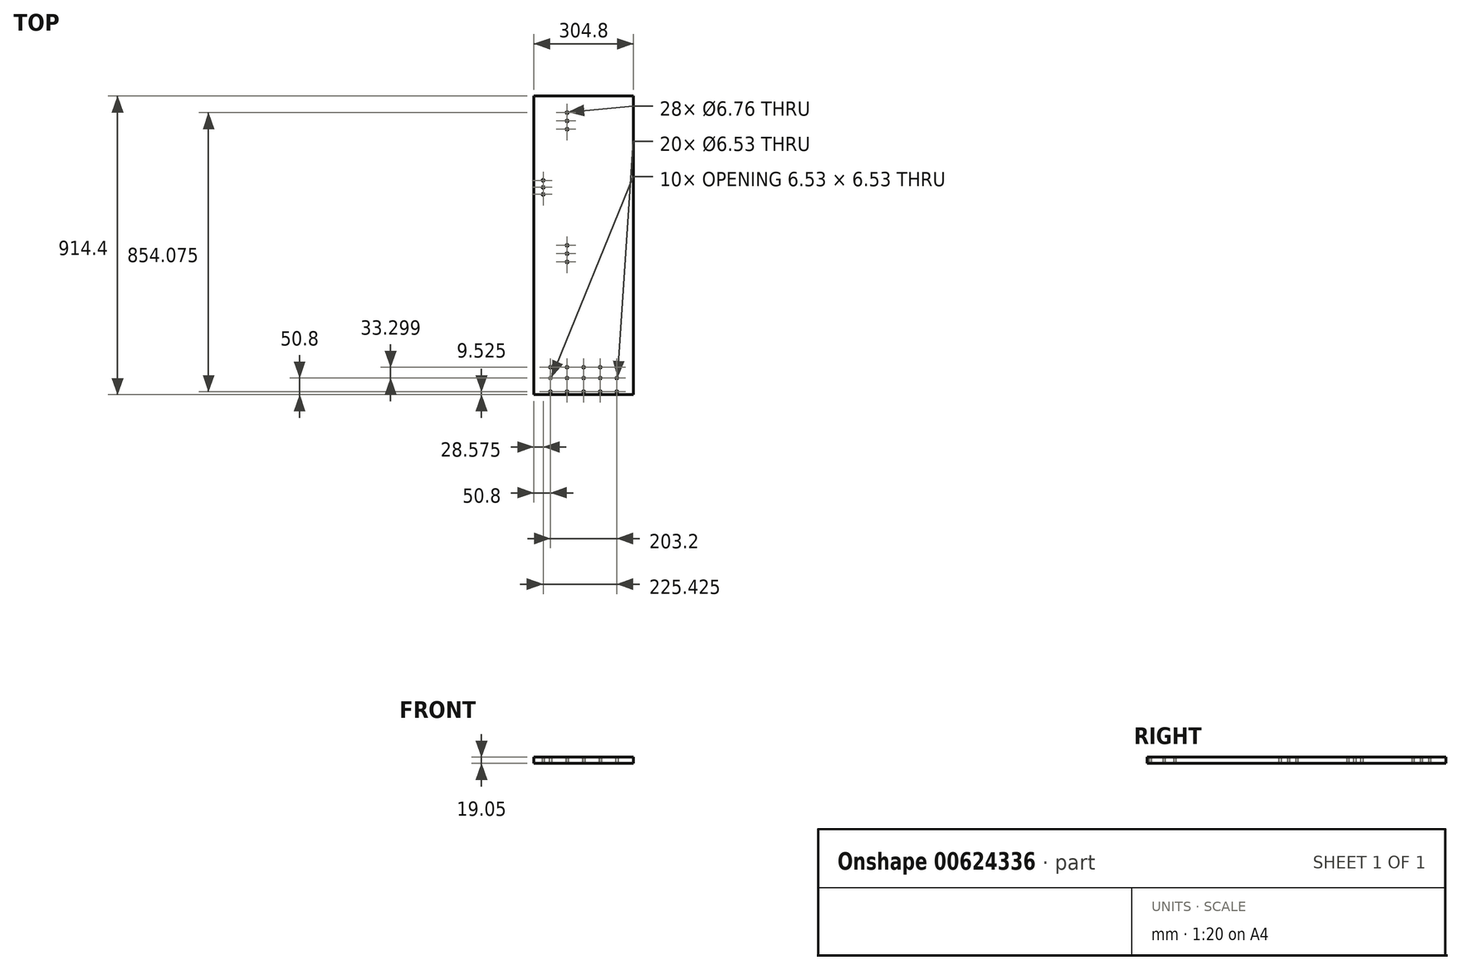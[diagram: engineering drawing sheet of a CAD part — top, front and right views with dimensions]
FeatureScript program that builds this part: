
annotation { "Feature Type Name" : "Feature", "Feature Type Description" : "" }
export const myFeature = defineFeature(function(context is Context, id is Id, definition is map)
    precondition{}
    {
        {
            var Q0;
            Q0=qCreatedBy(makeId("Top.planeOp"),FACE);
            var sketch = newSketch(context, id + "F0", { "sketchPlane" : qUnion([Q0])});
            skLineSegment(sketch, "E0.bottom", {"start": v(0, 0) * mm, "end": v(-304.8, 0) * mm});
            skLineSegment(sketch, "E0.top", {"start": v(0, 914.4) * mm, "end": v(-304.8, 914.4) * mm});
            skLineSegment(sketch, "E0.left", {"start": v(0, 0) * mm, "end": v(0, 914.4) * mm});
            skLineSegment(sketch, "E0.right", {"start": v(-304.8, 0) * mm, "end": v(-304.8, 914.4) * mm});
            skLineSegment(sketch, "E1", {"start": v(-203.2, 914.4) * mm, "end": v(-203.2, 0) * mm, "construction": true});
            skLineSegment(sketch, "E2", {"start": v(-304.8, 635) * mm, "end": v(0, 635) * mm, "construction": true});
            skCircle(sketch, "E3", {"center": v(-203.2, 863.6) * mm, "radius": 3.38 * mm});
            skCircle(sketch, "E4", {"center": v(-203.2, 838.2) * mm, "radius": 3.38 * mm});
            skCircle(sketch, "E5", {"center": v(-203.2, 812.8) * mm, "radius": 3.38 * mm});
            skCircle(sketch, "E6", {"center": v(-203.2, 457.2) * mm, "radius": 3.38 * mm});
            skCircle(sketch, "E7", {"center": v(-203.2, 431.8) * mm, "radius": 3.38 * mm});
            skCircle(sketch, "E8", {"center": v(-203.2, 406.4) * mm, "radius": 3.38 * mm});
            skLineSegment(sketch, "E9", {"start": v(-304.8, 9.52) * mm, "end": v(0, 9.52) * mm, "construction": true});
            skCircle(sketch, "E10", {"center": v(-254, 9.52) * mm, "radius": 3.38 * mm});
            skCircle(sketch, "E11.1.0.0", {"center": v(-203.2, 9.52) * mm, "radius": 3.38 * mm});
            skCircle(sketch, "E11.2.0.0", {"center": v(-152.4, 9.53) * mm, "radius": 3.38 * mm});
            skCircle(sketch, "E11.3.0.0", {"center": v(-101.6, 9.53) * mm, "radius": 3.38 * mm});
            skCircle(sketch, "E11.4.0.0", {"center": v(-50.8, 9.53) * mm, "radius": 3.38 * mm});
            skLineSegment(sketch, "E11.direction1", {"start": v(-254, 9.52) * mm, "end": v(-203.2, 9.52) * mm, "construction": true});
            skCircle(sketch, "E12", {"center": v(-276.23, 635) * mm, "radius": 3.38 * mm});
            skCircle(sketch, "E13", {"center": v(-276.23, 656.43) * mm, "radius": 3.38 * mm});
            skCircle(sketch, "E14", {"center": v(-276.23, 613.57) * mm, "radius": 3.38 * mm});
            skSolve(sketch);
        }
        {
            var Q0;
            Q0=makeQuery(id+"F0.imprint","IMPRINT",FACE,{"disambiguationData":[TD([[makeQuery(id+"F0.imprint","IMPRINT",EDGE,{"derivedFrom":sQuery(id+"F0.wireOp",EDGE,"E0.bottom")}),-1.0]])]});
            extrude(context, id + "F1", {"entities" : qUnion([Q0]), "depth" : 19.05 * mm, "offsetDistance" : 25.4 * mm});
        }
        {
            var Q0;
            Q0=makeQuery(id+"F1.opExtrude","CAP_FACE",FACE,{"disambiguationData":[OSD([sQuery(id+"F0.wireOp",EDGE,"E0.bottom"),sQuery(id+"F0.wireOp",EDGE,"E0.top"),sQuery(id+"F0.wireOp",EDGE,"E0.left"),sQuery(id+"F0.wireOp",EDGE,"E0.right"),sQuery(id+"F0.wireOp",EDGE,"E3"),sQuery(id+"F0.wireOp",EDGE,"E4"),sQuery(id+"F0.wireOp",EDGE,"E5"),sQuery(id+"F0.wireOp",EDGE,"E6"),sQuery(id+"F0.wireOp",EDGE,"E7"),sQuery(id+"F0.wireOp",EDGE,"E8"),sQuery(id+"F0.wireOp",EDGE,"E10"),sQuery(id+"F0.wireOp",EDGE,"E11.1.0.0"),sQuery(id+"F0.wireOp",EDGE,"E11.2.0.0"),sQuery(id+"F0.wireOp",EDGE,"E11.3.0.0"),sQuery(id+"F0.wireOp",EDGE,"E11.4.0.0")])],"isStart":true});
            var sketch = newSketch(context, id + "F2", { "sketchPlane" : qUnion([Q0])});
            skPoint(sketch, "E15", {"position": v(-50.8, -50.8) * mm});
            skPoint(sketch, "E16.0.1.0", {"position": v(-50.8, -84.1) * mm});
            skPoint(sketch, "E16.1.0.0", {"position": v(-101.6, -50.8) * mm});
            skPoint(sketch, "E16.1.1.0", {"position": v(-101.6, -84.1) * mm});
            skPoint(sketch, "E16.2.0.0", {"position": v(-152.4, -50.8) * mm});
            skPoint(sketch, "E16.2.1.0", {"position": v(-152.4, -84.1) * mm});
            skPoint(sketch, "E16.3.0.0", {"position": v(-203.2, -50.8) * mm});
            skPoint(sketch, "E16.3.1.0", {"position": v(-203.2, -84.1) * mm});
            skPoint(sketch, "E16.4.0.0", {"position": v(-254, -50.8) * mm});
            skPoint(sketch, "E16.4.1.0", {"position": v(-254, -84.1) * mm});
            skLineSegment(sketch, "E16.direction1", {"start": v(-50.8, -50.8) * mm, "end": v(-101.6, -50.8) * mm, "construction": true});
            skLineSegment(sketch, "E16.direction2", {"start": v(-50.8, -50.8) * mm, "end": v(-50.8, -84.1) * mm, "construction": true});
            skSolve(sketch);
        }
        {
            var Q0;
            Q0=sQuery(id+"F2.wireOp",VERTEX,"E16.0.1.0");
            var Q1;
            Q1=sQuery(id+"F2.wireOp",VERTEX,"E15");
            var Q2;
            Q2=sQuery(id+"F2.wireOp",VERTEX,"E16.1.0.0");
            var Q3;
            Q3=sQuery(id+"F2.wireOp",VERTEX,"E16.1.1.0");
            var Q4;
            Q4=sQuery(id+"F2.wireOp",VERTEX,"E16.2.1.0");
            var Q5;
            Q5=sQuery(id+"F2.wireOp",VERTEX,"E16.2.0.0");
            var Q6;
            Q6=sQuery(id+"F2.wireOp",VERTEX,"E16.3.1.0");
            var Q7;
            Q7=sQuery(id+"F2.wireOp",VERTEX,"E16.3.0.0");
            var Q8;
            Q8=sQuery(id+"F2.wireOp",VERTEX,"E16.4.1.0");
            var Q9;
            Q9=sQuery(id+"F2.wireOp",VERTEX,"E16.4.0.0");
            var Q10;
            Q10=makeQuery(id+"F1.opExtrude","SWEPT_BODY",BODY,{"disambiguationData":[OSD([sQuery(id+"F0.wireOp",EDGE,"E0.bottom"),sQuery(id+"F0.wireOp",EDGE,"E0.top"),sQuery(id+"F0.wireOp",EDGE,"E0.left"),sQuery(id+"F0.wireOp",EDGE,"E0.right"),sQuery(id+"F0.wireOp",EDGE,"E3"),sQuery(id+"F0.wireOp",EDGE,"E4"),sQuery(id+"F0.wireOp",EDGE,"E5"),sQuery(id+"F0.wireOp",EDGE,"E6"),sQuery(id+"F0.wireOp",EDGE,"E7"),sQuery(id+"F0.wireOp",EDGE,"E8"),sQuery(id+"F0.wireOp",EDGE,"E10"),sQuery(id+"F0.wireOp",EDGE,"E11.1.0.0"),sQuery(id+"F0.wireOp",EDGE,"E11.2.0.0"),sQuery(id+"F0.wireOp",EDGE,"E11.3.0.0"),sQuery(id+"F0.wireOp",EDGE,"E11.4.0.0")])]});
            hole(context, id + "F3", {"style" : HoleStyle.SIMPLE, "endStyle" : HoleEndStyle.THROUGH, "standardTappedOrClearance" : lookupTablePath({ "standard" : "ANSI", "fit" : "Close", "size" : "1/4", "type" : "Clearance" }), "standardBlindInLast" : lookupTablePath({ "fit" : "Close", "standard" : "ANSI", "size" : "1/4", "type" : "Clearance" }), "holeDiameter" : 6.53 * mm, "majorDiameter" : 6.35 * mm, "isTappedThrough" : true, "tappedDepth" : 12.7 * mm, "tapClearance" : 3, "startFromSketch" : true, "locations" : qUnion([Q0, Q1, Q2, Q3, Q4, Q5, Q6, Q7, Q8, Q9]), "scope" : qUnion([Q10])});
        }
        {
            var Q0;
            Q0=makeQuery(id+"F1.opExtrude","CAP_FACE",FACE,{"disambiguationData":[OSD([sQuery(id+"F0.wireOp",EDGE,"E0.bottom"),sQuery(id+"F0.wireOp",EDGE,"E0.top"),sQuery(id+"F0.wireOp",EDGE,"E0.left"),sQuery(id+"F0.wireOp",EDGE,"E0.right"),sQuery(id+"F0.wireOp",EDGE,"E3"),sQuery(id+"F0.wireOp",EDGE,"E4"),sQuery(id+"F0.wireOp",EDGE,"E5"),sQuery(id+"F0.wireOp",EDGE,"E6"),sQuery(id+"F0.wireOp",EDGE,"E7"),sQuery(id+"F0.wireOp",EDGE,"E8"),sQuery(id+"F0.wireOp",EDGE,"E10"),sQuery(id+"F0.wireOp",EDGE,"E11.1.0.0"),sQuery(id+"F0.wireOp",EDGE,"E11.2.0.0"),sQuery(id+"F0.wireOp",EDGE,"E11.3.0.0"),sQuery(id+"F0.wireOp",EDGE,"E11.4.0.0")])],"isStart":false});
            var sketch = newSketch(context, id + "F4", { "sketchPlane" : qUnion([Q0])});
            skLineSegment(sketch, "E17", {"start": v(-152.4, 84.1) * mm, "end": v(-152.4, 50.8) * mm, "construction": true});
            skPoint(sketch, "E18", {"position": v(-152.4, 67.45) * mm});
            skSolve(sketch);
        }
    });
